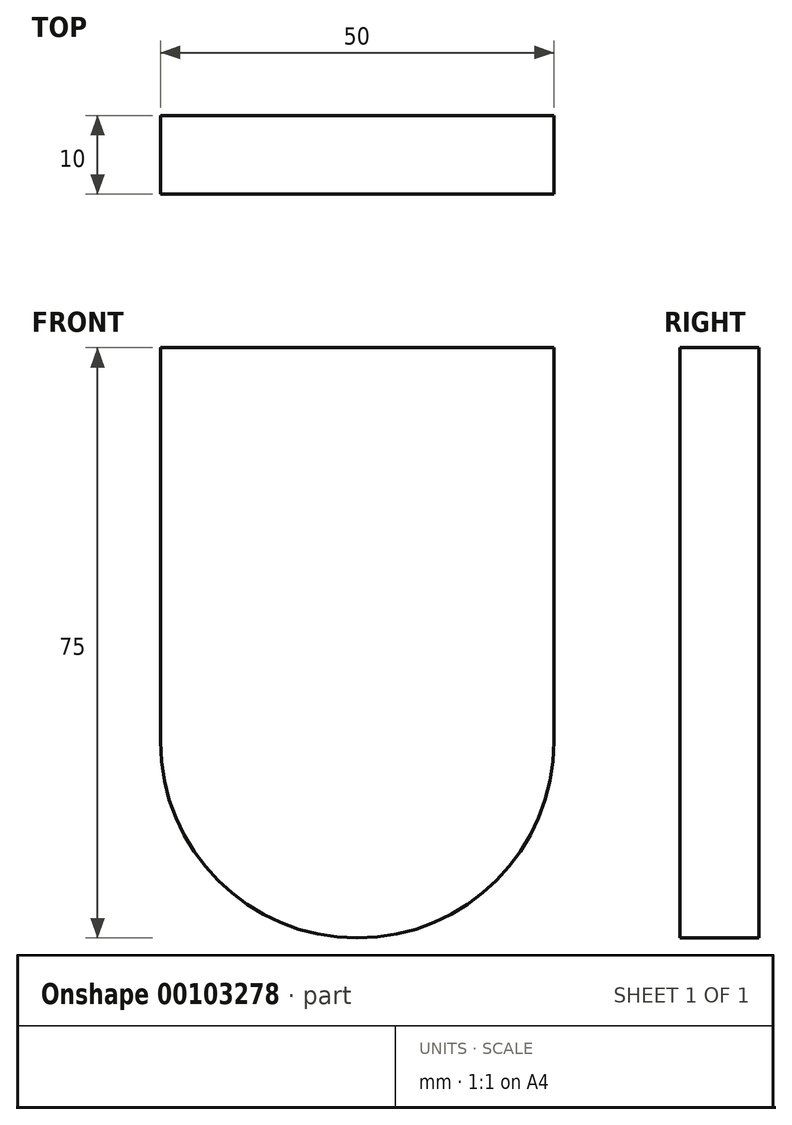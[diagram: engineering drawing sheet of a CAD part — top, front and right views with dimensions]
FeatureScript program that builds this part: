
annotation { "Feature Type Name" : "Feature", "Feature Type Description" : "" }
export const myFeature = defineFeature(function(context is Context, id is Id, definition is map)
    precondition{}
    {
        {
            var Q0;
            Q0=qCreatedBy(makeId("Front.planeOp"),FACE);
            var sketch = newSketch(context, id + "F0", { "sketchPlane" : qUnion([Q0])});
            skCircle(sketch, "E0", {"center": v(0, 0) * mm, "radius": 25 * mm});
            skLineSegment(sketch, "E1.bottom", {"start": v(-25, 50) * mm, "end": v(25, 50) * mm});
            skLineSegment(sketch, "E1.top", {"start": v(-25, 0) * mm, "end": v(25, 0) * mm});
            skLineSegment(sketch, "E1.left", {"start": v(-25, 50) * mm, "end": v(-25, 0) * mm});
            skLineSegment(sketch, "E1.right", {"start": v(25, 50) * mm, "end": v(25, 0) * mm});
            skSolve(sketch);
        }
        {
            var Q0;
            Q0=makeQuery(id+"F0.imprint","IMPRINT",FACE,{"disambiguationData":[TD([[makeQuery(id+"F0.imprint","IMPRINT",EDGE,{"derivedFrom":sQuery(id+"F0.wireOp",EDGE,"E1.bottom")}),-1.0]])]});
            var Q1;
            {var subQ0=sQuery(id+"F0.wireOp",EDGE,"E1.top");Q1=makeQuery(id+"F0.imprint","IMPRINT",FACE,{"disambiguationData":[TD([[makeQuery(id+"F0.imprint","IMPRINT",EDGE,{"derivedFrom":subQ0}),1.0]])]});}
            var Q2;
            {var subQ0=sQuery(id+"F0.wireOp",EDGE,"E1.top");Q2=makeQuery(id+"F0.imprint","IMPRINT",FACE,{"disambiguationData":[TD([[makeQuery(id+"F0.imprint","IMPRINT",EDGE,{"derivedFrom":subQ0}),-1.0]])]});}
            extrude(context, id + "F1", {"entities" : qUnion([Q0, Q1, Q2]), "endBound" : BoundingType.SYMMETRIC, "depth" : 10 * mm});
        }
    });
